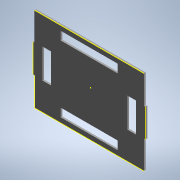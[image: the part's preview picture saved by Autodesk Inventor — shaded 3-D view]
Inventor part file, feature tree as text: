
AUTODESK INVENTOR PART (.ipt)
format: ipt  version: 2020 (Build 240168000, 168)  size: 176,640 bytes
history: native  units: mm (DEFAULTED — no unit token found)
features: sketch x15, extrude x10
ambient origin geometry x8: Origin, YZ Plane, XZ Plane, XY Plane, X Axis, Y Axis, Z Axis, Center Point
bodies: Solid1 (feature_tree)
feature tree (25):
  extrude  "Extrusion1"  Depth=3.0mm TaperAngle=0.0deg
  sketch  "Sketch2"  dims[d17=3.0mm d18=50.0mm]
  sketch  "Sketch3"  dims[d19=3.0mm d20=0.0mm d21=50.0mm]
  extrude  "Extrusion2"  Depth=50.0mm
  extrude  "Extrusion3"  Depth=50.0mm
  extrude  "Extrusion4"  Depth=3.0mm TaperAngle=0.0deg
  extrude  "Extrusion5"  Depth=3.0mm
  extrude  "Extrusion6"  Depth=15.0mm
  sketch  "Sketch9"  dims[d120=3.0mm d121=0.0mm d122=3.0mm d123=0.0mm]
  extrude  "Extrusion7"  Depth=3.0mm TaperAngle=0.0deg
  sketch  "Sketch11"
  extrude  "Extrusion8"  Depth=3.0mm TaperAngle=0.0deg
  extrude  "Extrusion9"  Depth=3.0mm TaperAngle=0.0deg
  extrude  "Extrusion10"  Depth=0.872665mm
  sketch  "Sketch15"
  sketch  "Sketch1"  dims[d2=3.0mm d3=0.0mm d15=3.0mm d16=0.0mm]
  sketch  "Sketch4"  dims[d22=3.0mm d23=3.0mm d24=0.0mm]
  sketch  "Sketch5"  dims[d25=50.0mm d26=3.0mm]
  sketch  "Sketch6"  dims[d27=3.0mm d28=0.0mm d32=15.0mm]
  sketch  "Sketch7"  dims[d33=30.0mm d34=3.0mm d35=0.0mm]
  sketch  "Sketch8"  dims[d36=30.0mm d37=0.0mm d77=3.0mm d78=0.0mm]
  sketch  "Sketch10"  dims[d124=5.0mm d125=0.872665mm]
  sketch  "Sketch12"
  sketch  "Sketch13"
  sketch  "Sketch14"
